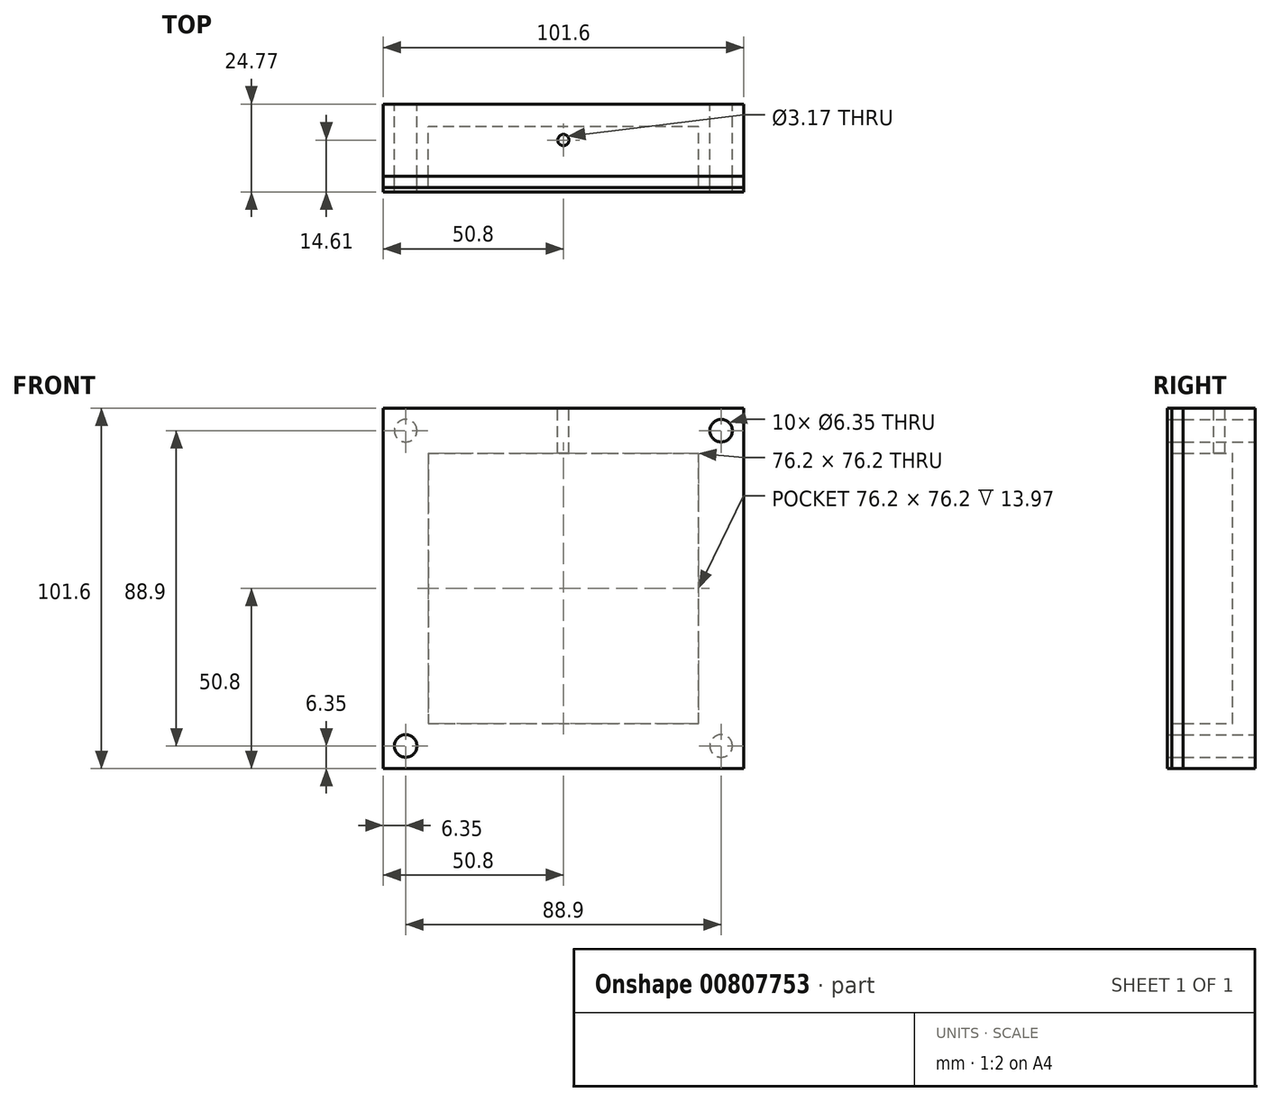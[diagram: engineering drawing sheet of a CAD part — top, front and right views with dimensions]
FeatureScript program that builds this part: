
annotation { "Feature Type Name" : "Feature", "Feature Type Description" : "" }
export const myFeature = defineFeature(function(context is Context, id is Id, definition is map)
    precondition{}
    {
        {
            var Q0;
            Q0=qCreatedBy(makeId("Front.planeOp"),FACE);
            var sketch = newSketch(context, id + "F0", { "sketchPlane" : qUnion([Q0])});
            skLineSegment(sketch, "E0", {"start": v(38.1, 0) * mm, "end": v(38.1, 38.1) * mm});
            skLineSegment(sketch, "E1.MirrorCS", {"start": v(38.1, 0) * mm, "end": v(38.1, -38.1) * mm});
            skLineSegment(sketch, "E2.MirrorCS", {"start": v(-38.1, 0) * mm, "end": v(-38.1, 38.1) * mm});
            skLineSegment(sketch, "E3.MirrorCS", {"start": v(-38.1, 0) * mm, "end": v(-38.1, -38.1) * mm});
            skLineSegment(sketch, "E4", {"start": v(-38.1, -38.1) * mm, "end": v(38.1, -38.1) * mm});
            skLineSegment(sketch, "E5", {"start": v(-38.1, 38.1) * mm, "end": v(38.1, 38.1) * mm});
            skLineSegment(sketch, "E6", {"start": v(38.1, 38.1) * mm, "end": v(50.8, 38.1) * mm});
            skLineSegment(sketch, "E7", {"start": v(50.8, 38.1) * mm, "end": v(50.8, -50.8) * mm});
            skLineSegment(sketch, "E8", {"start": v(50.8, -50.8) * mm, "end": v(-50.8, -50.8) * mm});
            skLineSegment(sketch, "E9", {"start": v(-50.8, -50.8) * mm, "end": v(-50.8, 50.8) * mm});
            skLineSegment(sketch, "E10", {"start": v(-50.8, 50.8) * mm, "end": v(50.8, 50.8) * mm});
            skLineSegment(sketch, "E11", {"start": v(50.8, 50.8) * mm, "end": v(50.8, 38.1) * mm});
            skLineSegment(sketch, "E12", {"start": v(-38.1, 38.1) * mm, "end": v(-38.1, 50.8) * mm});
            skLineSegment(sketch, "E13", {"start": v(-38.1, 50.8) * mm, "end": v(38.1, 50.8) * mm});
            skLineSegment(sketch, "E14", {"start": v(38.1, 50.8) * mm, "end": v(38.1, 38.1) * mm});
            skLineSegment(sketch, "E15", {"start": v(-50.8, 38.1) * mm, "end": v(-38.1, 38.1) * mm});
            skLineSegment(sketch, "E16", {"start": v(-38.1, 0) * mm, "end": v(-28.53, 0) * mm});
            skLineSegment(sketch, "E17", {"start": v(0, 38.1) * mm, "end": v(0, 29.89) * mm});
            skPoint(sketch, "E18", {"position": v(-44.45, 44.45) * mm});
            skPoint(sketch, "E18.positionSnap0", {"position": v(-38.1, 44.45) * mm});
            skPoint(sketch, "E18.positionSnap1", {"position": v(-44.45, 38.1) * mm});
            skCircle(sketch, "E19", {"center": v(-44.45, 44.45) * mm, "radius": 3.18 * mm});
            skCircle(sketch, "E20.MirrorC", {"center": v(44.45, 44.45) * mm, "radius": 3.18 * mm});
            skCircle(sketch, "E21.MirrorC", {"center": v(-44.45, -44.45) * mm, "radius": 3.18 * mm});
            skCircle(sketch, "E22.MirrorC", {"center": v(44.45, -44.45) * mm, "radius": 3.18 * mm});
            skSolve(sketch);
        }
        {
            var Q0;
            Q0=makeQuery(id+"F0.imprint","IMPRINT",FACE,{"disambiguationData":[TD([[makeQuery(id+"F0.imprint","IMPRINT",EDGE,{"derivedFrom":sQuery(id+"F0.wireOp",EDGE,"E0")}),-1.0]])]});
            var Q1;
            {var subQ1=sQuery(id+"F0.wireOp",EDGE,"E0");Q1=makeQuery(id+"F0.imprint","IMPRINT",FACE,{"disambiguationData":[TD([[makeQuery(id+"F0.imprint","IMPRINT",EDGE,{"derivedFrom":subQ1}),1.0]])]});}
            var Q2;
            {var subQ0=sQuery(id+"F0.wireOp",EDGE,"E12");Q2=makeQuery(id+"F0.imprint","IMPRINT",FACE,{"disambiguationData":[TD([[makeQuery(id+"F0.imprint","IMPRINT",EDGE,{"derivedFrom":subQ0}),-1.0]])]});}
            var Q3;
            {var subQ4=sQuery(id+"F0.wireOp",EDGE,"E12");Q3=makeQuery(id+"F0.imprint","IMPRINT",FACE,{"disambiguationData":[TD([[makeQuery(id+"F0.imprint","IMPRINT",EDGE,{"derivedFrom":subQ4}),1.0]])]});}
            var Q4;
            Q4=makeQuery(id+"F0.imprint","IMPRINT",FACE,{"disambiguationData":[TD([[makeQuery(id+"F0.imprint","IMPRINT",EDGE,{"derivedFrom":sQuery(id+"F0.wireOp",EDGE,"E6")}),1.0]])]});
            extrude(context, id + "F1", {"entities" : qUnion([Q0, Q1, Q2, Q3, Q4]), "depth" : 6.35 * mm, "offsetDistance" : 25.4 * mm});
        }
        {
            var Q0;
            Q0=makeQuery(id+"F0.imprint","IMPRINT",FACE,{"disambiguationData":[TD([[makeQuery(id+"F0.imprint","IMPRINT",EDGE,{"derivedFrom":sQuery(id+"F0.wireOp",EDGE,"E0")}),-1.0]])]});
            var Q1;
            {var subQ0=sQuery(id+"F0.wireOp",EDGE,"E12");Q1=makeQuery(id+"F0.imprint","IMPRINT",FACE,{"disambiguationData":[TD([[makeQuery(id+"F0.imprint","IMPRINT",EDGE,{"derivedFrom":subQ0}),-1.0]])]});}
            var Q2;
            Q2=makeQuery(id+"F0.imprint","IMPRINT",FACE,{"disambiguationData":[TD([[makeQuery(id+"F0.imprint","IMPRINT",EDGE,{"derivedFrom":sQuery(id+"F0.wireOp",EDGE,"E6")}),1.0]])]});
            var Q3;
            {var subQ4=sQuery(id+"F0.wireOp",EDGE,"E12");Q3=makeQuery(id+"F0.imprint","IMPRINT",FACE,{"disambiguationData":[TD([[makeQuery(id+"F0.imprint","IMPRINT",EDGE,{"derivedFrom":subQ4}),1.0]])]});}
            var Q4;
            Q4 = qSketchRegion(id + "F3", true);
            extrude(context, id + "F2", {"entities" : qUnion([Q0, Q1, Q2, Q3, Q4]), "operationType" : NewBodyOperationType.ADD, "depth" : 20.32 * mm, "offsetDistance" : 25.4 * mm});
        }
        {
            var Q0;
            {var subQ0=sQuery(id+"F0.wireOp",EDGE,"E10");Q0=makeQuery(id+"F2.boolean.opBoolean","MERGE",FACE,{"derivedFrom":[makeQuery(id+"F1.opExtrude","SWEPT_FACE",FACE,{"disambiguationData":[OSD([subQ0])]}),makeQuery(id+"F2.opExtrude","SWEPT_FACE",FACE,{"disambiguationData":[OSD([subQ0])]})]});}
            var sketch = newSketch(context, id + "F3", { "sketchPlane" : qUnion([Q0])});
            skLineSegment(sketch, "E23", {"start": v(-50.8, 0) * mm, "end": v(50.8, 0) * mm});
            skLineSegment(sketch, "E24", {"start": v(50.8, 0) * mm, "end": v(50.8, -20.32) * mm});
            skLineSegment(sketch, "E25", {"start": v(50.8, -20.32) * mm, "end": v(-50.8, -20.32) * mm});
            skLineSegment(sketch, "E26", {"start": v(-50.8, -20.32) * mm, "end": v(-50.8, 0) * mm});
            skCircle(sketch, "E27", {"center": v(0, -10.16) * mm, "radius": 1.59 * mm});
            skSolve(sketch);
        }
        {
            var Q0;
            Q0=makeQuery(id+"F3.imprint","IMPRINT",FACE,{"disambiguationData":[TD([[makeQuery(id+"F3.imprint","IMPRINT",EDGE,{"derivedFrom":sQuery(id+"F3.wireOp",EDGE,"E27")}),1.0]])]});
            extrude(context, id + "F4", {"entities" : qUnion([Q0]), "operationType" : NewBodyOperationType.REMOVE, "oppositeDirection" : true, "depth" : 25.4 * mm, "offsetDistance" : 25.4 * mm});
        }
        {
            var Q0;
            Q0=makeQuery(id+"F2.opExtrude","CAP_FACE",FACE,{"disambiguationData":[OSD([sQuery(id+"F0.wireOp",EDGE,"E0"),sQuery(id+"F0.wireOp",EDGE,"E1.MirrorCS"),sQuery(id+"F0.wireOp",EDGE,"E2.MirrorCS"),sQuery(id+"F0.wireOp",EDGE,"E3.MirrorCS"),sQuery(id+"F0.wireOp",EDGE,"E4"),sQuery(id+"F0.wireOp",EDGE,"E5"),sQuery(id+"F0.wireOp",EDGE,"E7"),sQuery(id+"F0.wireOp",EDGE,"E8"),sQuery(id+"F0.wireOp",EDGE,"E9"),sQuery(id+"F0.wireOp",EDGE,"E10"),sQuery(id+"F0.wireOp",EDGE,"E11"),sQuery(id+"F0.wireOp",EDGE,"E19"),sQuery(id+"F0.wireOp",EDGE,"E20.MirrorC"),sQuery(id+"F0.wireOp",EDGE,"E21.MirrorC"),sQuery(id+"F0.wireOp",EDGE,"E22.MirrorC")])],"isStart":false});
            var sketch = newSketch(context, id + "F5", { "sketchPlane" : qUnion([Q0])});
            skLineSegment(sketch, "E28", {"start": v(-50.8, 50.8) * mm, "end": v(50.8, 50.8) * mm});
            skLineSegment(sketch, "E29", {"start": v(50.8, 50.8) * mm, "end": v(50.8, -50.8) * mm});
            skLineSegment(sketch, "E30", {"start": v(50.8, -50.8) * mm, "end": v(-50.8, -50.8) * mm});
            skLineSegment(sketch, "E31", {"start": v(-50.8, -50.8) * mm, "end": v(-50.8, 50.8) * mm});
            skLineSegment(sketch, "E32", {"start": v(-38.1, 38.1) * mm, "end": v(38.1, 38.1) * mm});
            skLineSegment(sketch, "E33", {"start": v(38.1, 38.1) * mm, "end": v(38.1, -38.1) * mm});
            skLineSegment(sketch, "E34", {"start": v(38.1, -38.1) * mm, "end": v(-38.1, -38.1) * mm});
            skLineSegment(sketch, "E35", {"start": v(-38.1, -38.1) * mm, "end": v(-38.1, 38.1) * mm});
            skSolve(sketch);
        }
        {
            var Q0;
            Q0=makeQuery(id+"F5.imprint","IMPRINT",FACE,{"disambiguationData":[TD([[makeQuery(id+"F5.imprint","IMPRINT",EDGE,{"derivedFrom":sQuery(id+"F5.wireOp",EDGE,"E28")}),-1.0]])]});
            extrude(context, id + "F6", {"entities" : qUnion([Q0]), "depth" : 3.17 * mm, "offsetDistance" : 25.4 * mm});
        }
        {
            var Q0;
            Q0=makeQuery(id+"F6.opExtrude","CAP_FACE",FACE,{"disambiguationData":[OSD([sQuery(id+"F0.wireOp",EDGE,"E19"),sQuery(id+"F0.wireOp",EDGE,"E20.MirrorC"),sQuery(id+"F0.wireOp",EDGE,"E21.MirrorC"),sQuery(id+"F0.wireOp",EDGE,"E22.MirrorC"),sQuery(id+"F5.wireOp",EDGE,"E28"),sQuery(id+"F5.wireOp",EDGE,"E29"),sQuery(id+"F5.wireOp",EDGE,"E30"),sQuery(id+"F5.wireOp",EDGE,"E31"),sQuery(id+"F5.wireOp",EDGE,"E32"),sQuery(id+"F5.wireOp",EDGE,"E33"),sQuery(id+"F5.wireOp",EDGE,"E34"),sQuery(id+"F5.wireOp",EDGE,"E35")])],"isStart":false});
            var sketch = newSketch(context, id + "F7", { "sketchPlane" : qUnion([Q0])});
            skLineSegment(sketch, "E36", {"start": v(-50.8, 50.8) * mm, "end": v(50.8, 50.8) * mm});
            skLineSegment(sketch, "E37", {"start": v(50.8, 50.8) * mm, "end": v(50.8, -50.8) * mm});
            skLineSegment(sketch, "E38", {"start": v(50.8, -50.8) * mm, "end": v(-50.8, -50.8) * mm});
            skLineSegment(sketch, "E39", {"start": v(-50.8, -50.8) * mm, "end": v(-50.8, 50.8) * mm});
            skSolve(sketch);
        }
        {
            var Q0;
            Q0=makeQuery(id+"F7.imprint","IMPRINT",FACE,{"disambiguationData":[TD([[makeQuery(id+"F7.imprint","IMPRINT",EDGE,{"derivedFrom":sQuery(id+"F7.wireOp",EDGE,"E36")}),-1.0]])]});
            var Q1;
            Q1=makeQuery(id+"F7.imprint","IMPRINT",FACE,{"disambiguationData":[TD([[makeQuery(id+"F7.imprint","IMPRINT",EDGE,{"derivedFrom":makeQuery(id+"F6.opExtrude","CAP_EDGE",EDGE,{"disambiguationData":[OSD([sQuery(id+"F5.wireOp",EDGE,"E32")])],"isStart":false})}),-1.0]])]});
            var Q2;
            Q2=makeQuery(id+"F7.imprint","IMPRINT",FACE,{"disambiguationData":[TD([[makeQuery(id+"F7.imprint","IMPRINT",EDGE,{"derivedFrom":makeQuery(id+"F6.opExtrude","CAP_EDGE",EDGE,{"disambiguationData":[OSD([sQuery(id+"F0.wireOp",EDGE,"E19")])],"isStart":false})}),1.0]])]});
            var Q3;
            Q3=makeQuery(id+"F7.imprint","IMPRINT",FACE,{"disambiguationData":[TD([[makeQuery(id+"F7.imprint","IMPRINT",EDGE,{"derivedFrom":makeQuery(id+"F6.opExtrude","CAP_EDGE",EDGE,{"disambiguationData":[OSD([sQuery(id+"F0.wireOp",EDGE,"E20.MirrorC")])],"isStart":false})}),-1.0]])]});
            var Q4;
            Q4=makeQuery(id+"F7.imprint","IMPRINT",FACE,{"disambiguationData":[TD([[makeQuery(id+"F7.imprint","IMPRINT",EDGE,{"derivedFrom":makeQuery(id+"F6.opExtrude","CAP_EDGE",EDGE,{"disambiguationData":[OSD([sQuery(id+"F0.wireOp",EDGE,"E22.MirrorC")])],"isStart":false})}),1.0]])]});
            var Q5;
            Q5=makeQuery(id+"F7.imprint","IMPRINT",FACE,{"disambiguationData":[TD([[makeQuery(id+"F7.imprint","IMPRINT",EDGE,{"derivedFrom":makeQuery(id+"F6.opExtrude","CAP_EDGE",EDGE,{"disambiguationData":[OSD([sQuery(id+"F0.wireOp",EDGE,"E21.MirrorC")])],"isStart":false})}),-1.0]])]});
            extrude(context, id + "F8", {"entities" : qUnion([Q0, Q1, Q2, Q3, Q4, Q5]), "depth" : 1.27 * mm, "offsetDistance" : 25.4 * mm});
        }
    });
